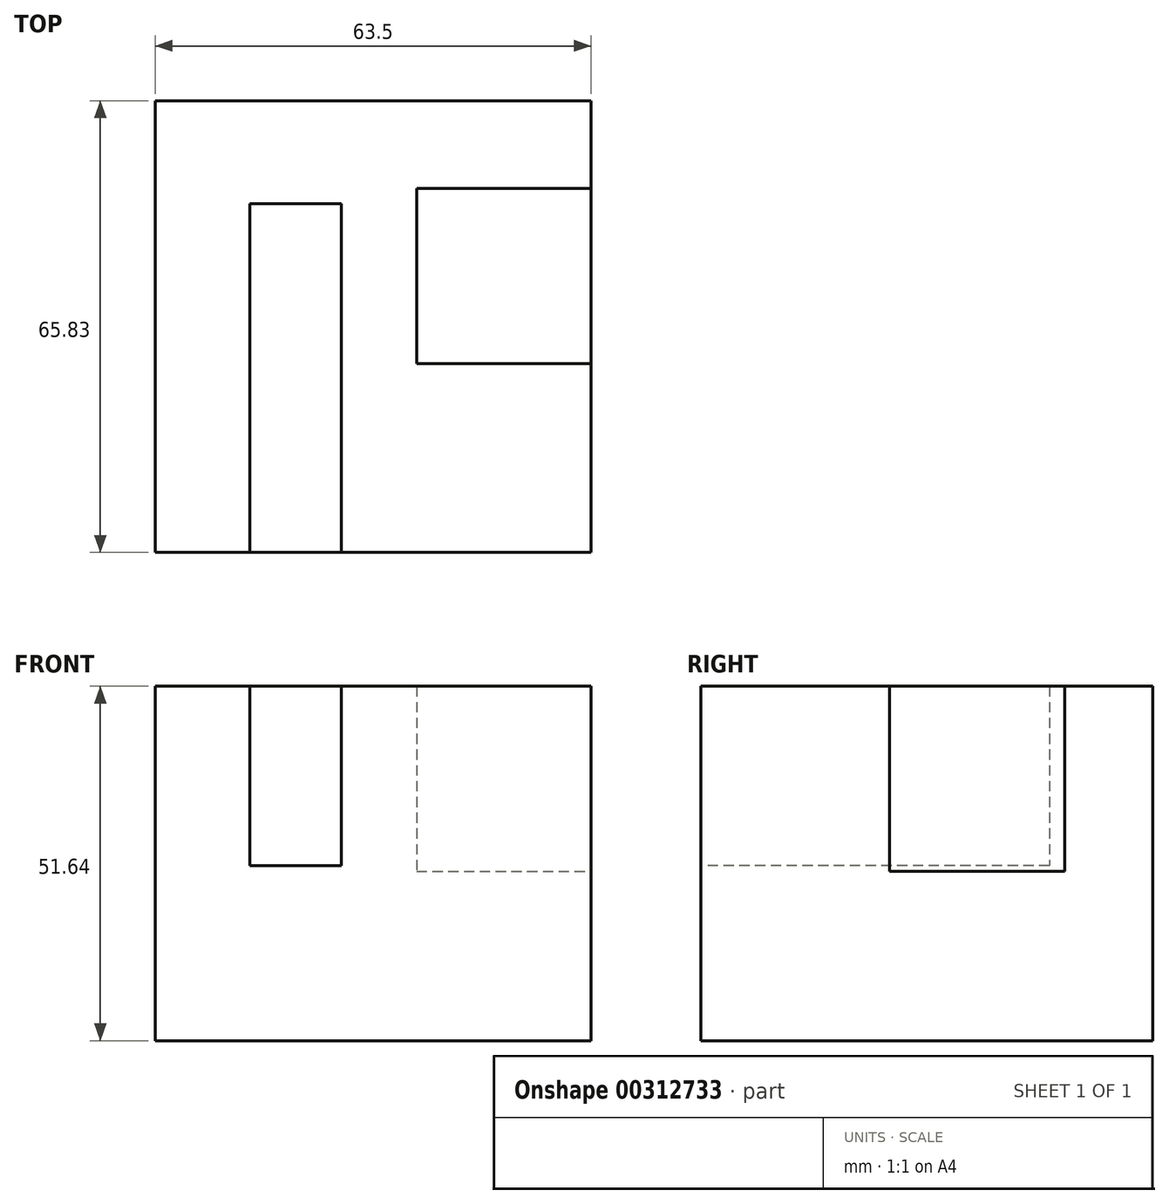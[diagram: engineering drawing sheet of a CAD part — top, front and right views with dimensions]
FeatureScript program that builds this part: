
annotation { "Feature Type Name" : "Feature", "Feature Type Description" : "" }
export const myFeature = defineFeature(function(context is Context, id is Id, definition is map)
    precondition{}
    {
        {
            var Q0;
            Q0=qCreatedBy(makeId("Right.planeOp"),FACE);
            var sketch = newSketch(context, id + "F0", { "sketchPlane" : qUnion([Q0])});
            skLineSegment(sketch, "E0", {"start": v(-56.04, 36.32) * mm, "end": v(-56.04, -15.32) * mm});
            skLineSegment(sketch, "E1", {"start": v(-56.04, -15.32) * mm, "end": v(9.79, -15.32) * mm});
            skLineSegment(sketch, "E2", {"start": v(9.79, -15.32) * mm, "end": v(9.79, 36.32) * mm});
            skLineSegment(sketch, "E3", {"start": v(9.79, 36.32) * mm, "end": v(-56.04, 36.32) * mm});
            skSolve(sketch);
        }
        {
            var Q0;
            Q0 = qSketchRegion(id + "F0", true);
            extrude(context, id + "F1", {"entities" : qUnion([Q0]), "depth" : 63.5 * mm});
        }
        {
            var Q0;
            Q0=makeQuery(id+"F1.opExtrude","CAP_FACE",FACE,{"disambiguationData":[OSD([sQuery(id+"F0.wireOp",EDGE,"E0"),sQuery(id+"F0.wireOp",EDGE,"E1"),sQuery(id+"F0.wireOp",EDGE,"E2"),sQuery(id+"F0.wireOp",EDGE,"E3")])],"isStart":false});
            var sketch = newSketch(context, id + "F2", { "sketchPlane" : qUnion([Q0])});
            skLineSegment(sketch, "E4", {"start": v(9.79, 36.32) * mm, "end": v(-2.98, 36.32) * mm});
            skLineSegment(sketch, "E5", {"start": v(-2.98, 36.32) * mm, "end": v(-2.98, 9.36) * mm});
            skLineSegment(sketch, "E6", {"start": v(-2.98, 9.36) * mm, "end": v(-28.51, 9.36) * mm});
            skLineSegment(sketch, "E7", {"start": v(-28.51, 9.36) * mm, "end": v(-28.51, 36.32) * mm});
            skLineSegment(sketch, "E8", {"start": v(-28.51, 36.32) * mm, "end": v(-2.98, 36.32) * mm});
            skSolve(sketch);
        }
        {
            var Q0;
            Q0=makeQuery(id+"F2.imprint","IMPRINT",FACE,{"disambiguationData":[TD([[makeQuery(id+"F2.imprint","IMPRINT",EDGE,{"derivedFrom":sQuery(id+"F2.wireOp",EDGE,"E5")}),-1.0]])]});
            extrude(context, id + "F3", {"entities" : qUnion([Q0]), "operationType" : NewBodyOperationType.REMOVE, "oppositeDirection" : true, "depth" : 25.4 * mm});
        }
        {
            var Q0;
            Q0=makeQuery(id+"F1.opExtrude","SWEPT_FACE",FACE,{"disambiguationData":[OSD([sQuery(id+"F0.wireOp",EDGE,"E0")])]});
            var sketch = newSketch(context, id + "F4", { "sketchPlane" : qUnion([Q0])});
            skLineSegment(sketch, "E9", {"start": v(0, 36.32) * mm, "end": v(13.76, 36.32) * mm});
            skLineSegment(sketch, "E10", {"start": v(13.76, 36.32) * mm, "end": v(13.76, 10.21) * mm});
            skLineSegment(sketch, "E11", {"start": v(13.76, 10.21) * mm, "end": v(27.1, 10.21) * mm});
            skLineSegment(sketch, "E12", {"start": v(27.1, 10.21) * mm, "end": v(27.1, 36.32) * mm});
            skLineSegment(sketch, "E13", {"start": v(27.1, 36.32) * mm, "end": v(13.76, 36.32) * mm});
            skSolve(sketch);
        }
        {
            var Q0;
            Q0=makeQuery(id+"F4.imprint","IMPRINT",FACE,{"disambiguationData":[TD([[makeQuery(id+"F4.imprint","IMPRINT",EDGE,{"derivedFrom":sQuery(id+"F4.wireOp",EDGE,"E10")}),1.0]])]});
            extrude(context, id + "F5", {"entities" : qUnion([Q0]), "operationType" : NewBodyOperationType.REMOVE, "oppositeDirection" : true, "depth" : 50.8 * mm});
        }
    });
